# Revit family: PRD_FrankeWS_WlHngWshBsns_AnimaWashbasin_CM700
name_source: partatom
category: Plumbing Fixtures
revit_build: Autodesk Revit 2018 (Build: 20190510_1515(x64)
units: mm (PartAtom-declared; Revit-internal decimal feet)

## family parameters
Cut with Voids When Loaded = No
Host = Face
OmniClass Number = 23.45.05.14.14
OmniClass Title = Sinks/Lavatories
Part Type = Normal
Room Calculation Point = No
Round Connector Dimension = Use Diameter
Shared = No

## types (1)
- CM700
    AssetType = Fixed
    BIMObjectName = PRD_AR_WallHungWashBasins_AnimaWashbasin_CM700
    Category = Pr_40_20_96_96, Wall-hung wash basins
    Color = Stainless steel
    Default Elevation = 850 mm  [stored 2.78871 ft]
    Description = Wash basin, stainless steel, surface satin finished, material thickness 1.0 mm, with tap ledge 95 mm, without tap hole, waste G 1 1/2 B, incl. screws and dowels. width 700 mm, with 1 basin 600x340x130 mm
    DrainSize = DN 40 (1 1/2 inch.)
    DurationUnit = year
    Features = stainless steel, 1.00 mm, satin finished, wall mounting, 700x170x514 mm (WxHxD)
    Finish = Satin finished
    Form = Wall hung wash basin
    GrossWeight = 8.00 kg
    IfcExportAs = IfcSanitaryTerminalType
    IfcExportType = WASHHANDBASIN
    IntegralAccessories = Incl. stainless steel screws and dowels
    Manufacturer = KWC Group AG
    ManufacturerName = KWC Group AG
    ManufacturerURL = www.kwc.com
    Material = Stainless steel
    MaterialsBody = Stainless steel 1.4301
    MaterialsFinishAndColour = Stainless steel, satin finished
    Model = CM700
    ModelNumber = 2000100039
    ModelReference = CM700
    NBSDescription = Wall hung wash basins
    NBSReference = 45-35-70/369
    Name = ANIMA wall-hung wash basin CM700
    NetWeight = 8.00 kg
    NominalDepth = 514 mm  [stored 1.68635 ft]
    NominalHeight = 170 mm  [stored 0.557743 ft]
    NominalLength = 0 mm  [stored 0 ft]
    NominalWidth = 700 mm  [stored 2.29659 ft]
    ProductInformation = https://pim.kwc.com
    Shape = Rectangular
    Size = 700 x 514 x 170 mm
    URL = www.kwc.com
    Uniclass2015Code = Pr_40_20_96_96
    Uniclass2015Title = Wall-hung wash basins
    Uniclass2015Version = Products v1.5
    Version = 1
    WarrantyDurationUnit = year
    WashHandBasinMounting = WallHung
    WashHandBasinType = HandRinse
    WashbasinMaterial = PRD_AR_StainlessSteel_SatinFinished
    WasteSize = 40  [stored 0.131234 ft]
    WaterSupplyOverflowAndWasteHolesOverflow = None
    WaterSupplyOverflowAndWasteHolesWaste = Center-Back
    WaterSupplyOverflowAndWasteHolesWaterSupply = No tapholes

note: [stored X ft] marks values corroborated as IEEE doubles in the binary element streams (Revit-internal decimal feet)

## geometry (parser evidence)
native form markers: Sweep x5
no freeform markers — native parametric forms only
